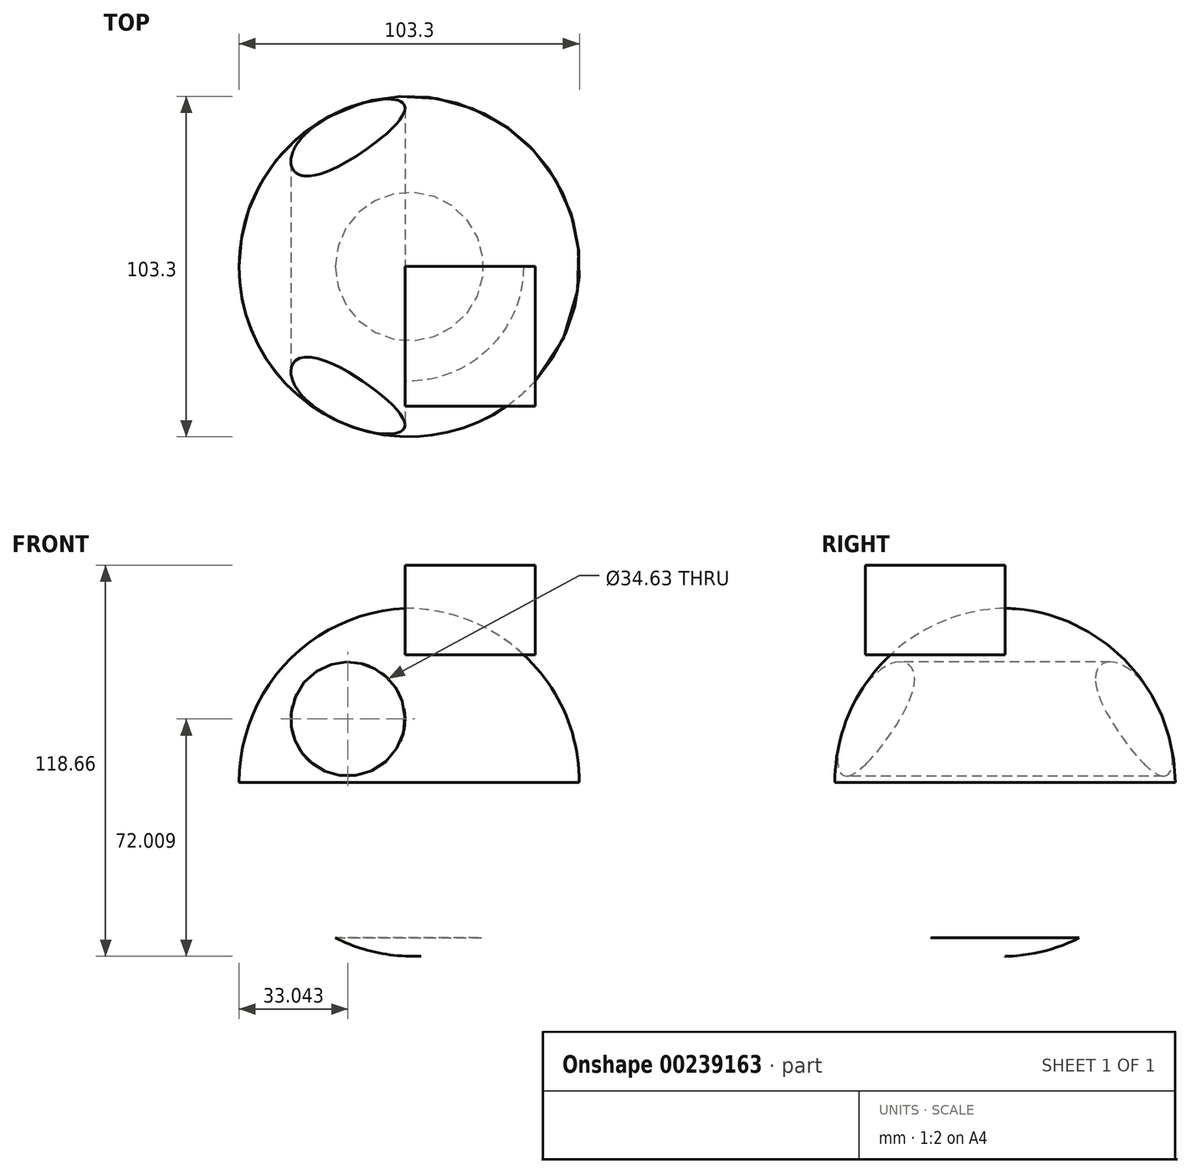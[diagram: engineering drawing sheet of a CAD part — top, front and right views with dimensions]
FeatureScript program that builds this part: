
annotation { "Feature Type Name" : "Feature", "Feature Type Description" : "" }
export const myFeature = defineFeature(function(context is Context, id is Id, definition is map)
    precondition{}
    {
        {
            var Q0;
            Q0=qCreatedBy(makeId("Front.planeOp"),FACE);
            var sketch = newSketch(context, id + "F0", { "sketchPlane" : qUnion([Q0])});
            skArc(sketch, "E0", {"start": v(2.35, -52.78) * mm, "mid": v(52.81, 1.18) * mm, "end": v(0, 52.83) * mm});
            skLineSegment(sketch, "E1", {"start": v(0, 52.83) * mm, "end": v(2.4, -54.98) * mm});
            skSolve(sketch);
        }
        {
            var Q0;
            {var subQ0=sQuery(id+"F0.wireOp",EDGE,"E0");Q0=makeQuery(id+"F0.imprint","IMPRINT",FACE,{"disambiguationData":[TD([[makeQuery(id+"F0.imprint","IMPRINT",EDGE,{"derivedFrom":subQ0}),1.0]])]});}
            var Q1;
            Q1=sQuery(id+"F0.wireOp",EDGE,"E1");
            revolve(context, id + "F1", {"entities" : qUnion([Q0]), "axis" : qUnion([Q1]), "revolveType" : RevolveType.FULL});
        }
        {
            var Q0;
            Q0=qCreatedBy(makeId("Front.planeOp"),FACE);
            var sketch = newSketch(context, id + "F2", { "sketchPlane" : qUnion([Q0])});
            skCircle(sketch, "E2", {"center": v(-17.43, 19.23) * mm, "radius": 17.31 * mm});
            skSolve(sketch);
        }
        {
            var Q0;
            Q0 = qSketchRegion(id + "F2", true);
            extrude(context, id + "F3", {"entities" : qUnion([Q0]), "operationType" : NewBodyOperationType.REMOVE, "endBound" : BoundingType.SYMMETRIC, "oppositeDirection" : true, "depth" : 168.6 * mm});
        }
        {
            var Q0;
            Q0=qCreatedBy(makeId("Front.planeOp"),FACE);
            var sketch = newSketch(context, id + "F4", { "sketchPlane" : qUnion([Q0])});
            skLineSegment(sketch, "E3.bottom", {"start": v(39.41, 65.88) * mm, "end": v(0, 65.88) * mm});
            skLineSegment(sketch, "E3.top", {"start": v(39.41, 38.77) * mm, "end": v(0, 38.77) * mm});
            skLineSegment(sketch, "E3.left", {"start": v(39.41, 65.88) * mm, "end": v(39.41, 38.77) * mm});
            skLineSegment(sketch, "E3.right", {"start": v(0, 65.88) * mm, "end": v(0, 38.77) * mm});
            skSolve(sketch);
        }
        {
            var Q0;
            Q0 = qSketchRegion(id + "F4", true);
            extrude(context, id + "F5", {"entities" : qUnion([Q0]), "operationType" : NewBodyOperationType.ADD, "depth" : 42.4 * mm});
        }
        {
            var Q0;
            Q0=qCreatedBy(makeId("Top.planeOp"),FACE);
            var sketch = newSketch(context, id + "F6", { "sketchPlane" : qUnion([Q0])});
            skCircle(sketch, "E4", {"center": v(0, 0) * mm, "radius": 88.6 * mm});
            skSolve(sketch);
        }
        {
            var Q0;
            Q0 = qSketchRegion(id + "F6", true);
            extrude(context, id + "F7", {"entities" : qUnion([Q0]), "operationType" : NewBodyOperationType.REMOVE, "oppositeDirection" : true, "depth" : 47.2 * mm});
        }
    });
